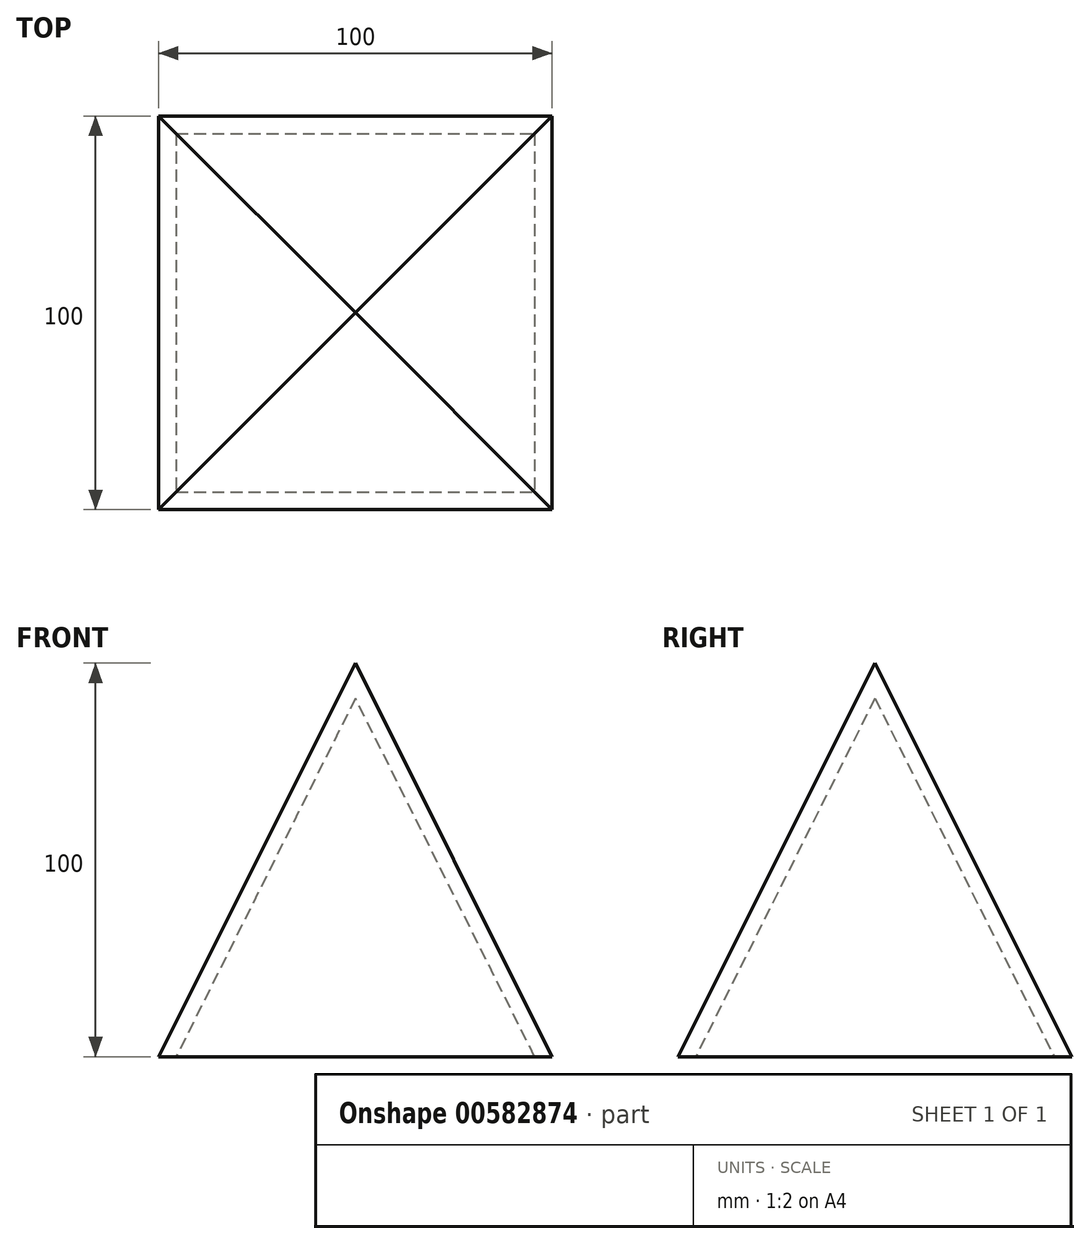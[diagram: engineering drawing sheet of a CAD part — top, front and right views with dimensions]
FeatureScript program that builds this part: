
annotation { "Feature Type Name" : "Feature", "Feature Type Description" : "" }
export const myFeature = defineFeature(function(context is Context, id is Id, definition is map)
    precondition{}
    {
        {
            var Q0;
            Q0=qCreatedBy(makeId("Top.planeOp"),FACE);
            var sketch = newSketch(context, id + "F0", { "sketchPlane" : qUnion([Q0])});
            skLineSegment(sketch, "E0.bottom", {"start": v(-50, 50) * mm, "end": v(50, 50) * mm});
            skLineSegment(sketch, "E0.top", {"start": v(-50, -50) * mm, "end": v(50, -50) * mm});
            skLineSegment(sketch, "E0.left", {"start": v(-50, 50) * mm, "end": v(-50, -50) * mm});
            skLineSegment(sketch, "E0.right", {"start": v(50, 50) * mm, "end": v(50, -50) * mm});
            skLineSegment(sketch, "E1", {"start": v(-50, 50) * mm, "end": v(50, -50) * mm, "construction": true});
            skSolve(sketch);
        }
        {
            var Q0;
            Q0=qCreatedBy(makeId("Top.planeOp"),FACE);
            cPlane(context, id + "F1", {"entities" : qUnion([Q0]), "cplaneType" : CPlaneType.OFFSET, "offset" : 100 * mm, "width" : 150 * mm, "height" : 150 * mm});
        }
        {
            var Q0;
            Q0=qCreatedBy(id+"F1.planeOp",FACE);
            var sketch = newSketch(context, id + "F2", { "sketchPlane" : qUnion([Q0])});
            skPoint(sketch, "E2", {"position": v(0, 0) * mm});
            skSolve(sketch);
        }
        {
            var Q0;
            Q0=makeQuery(id+"F0.imprint","IMPRINT",FACE,{"disambiguationData":[TD([[makeQuery(id+"F0.imprint","IMPRINT",EDGE,{"derivedFrom":sQuery(id+"F0.wireOp",EDGE,"E0.bottom")}),-1.0]])]});
            var Q1;
            Q1=sQuery(id+"F2.wireOp",VERTEX,"E2");
            loft(context, id + "F3", {"sheetProfilesArray" : [{ "sheetProfileEntities" : qUnion([Q0]) }, { "sheetProfileEntities" : qUnion([Q1]) }]});
        }
        {
            var Q0;
            Q0=makeQuery(id+"F3.opLoft","CAP_FACE",FACE,{"disambiguationData":[OSD([makeQuery(id+"F0.imprint","IMPRINT",FACE,{"disambiguationData":[TD([[makeQuery(id+"F0.imprint","IMPRINT",EDGE,{"derivedFrom":sQuery(id+"F0.wireOp",EDGE,"E0.bottom")}),-1.0]])]})])],"isStart":true});
            var Q1;
            Q1=makeQuery(id+"F3.opLoft","SWEPT_BODY",BODY,{"disambiguationData":[OSD([makeQuery(id+"F0.imprint","IMPRINT",FACE,{"disambiguationData":[TD([[makeQuery(id+"F0.imprint","IMPRINT",EDGE,{"derivedFrom":sQuery(id+"F0.wireOp",EDGE,"E0.bottom")}),-1.0]])]}),sQuery(id+"F2.wireOp",VERTEX,"E2")])]});
            shell(context, id + "F4", {"entities" : qUnion([Q0]), "parts" : qUnion([Q1]), "thickness" : 4 * mm});
        }
    });
